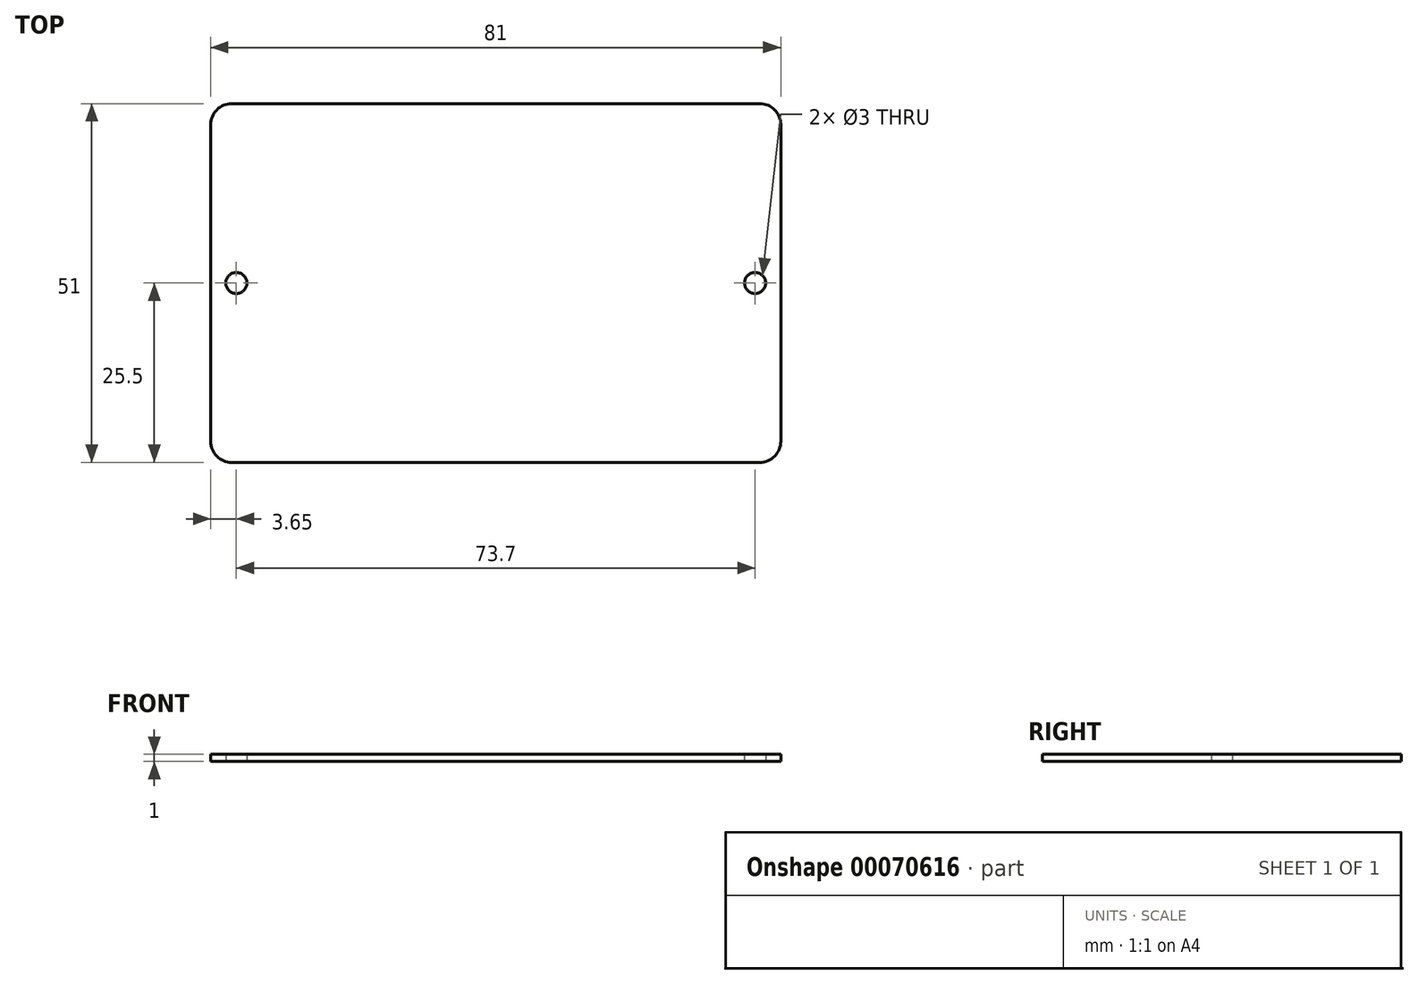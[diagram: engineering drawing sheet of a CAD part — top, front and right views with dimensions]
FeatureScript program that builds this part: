
annotation { "Feature Type Name" : "Feature", "Feature Type Description" : "" }
export const myFeature = defineFeature(function(context is Context, id is Id, definition is map)
    precondition{}
    {
        {
            var Q0;
            Q0=qCreatedBy(makeId("Top.planeOp"),FACE);
            var sketch = newSketch(context, id + "F0", { "sketchPlane" : qUnion([Q0])});
            skLineSegment(sketch, "E0.bottom", {"start": v(-37.5, 25.5) * mm, "end": v(37.5, 25.5) * mm});
            skLineSegment(sketch, "E0.top", {"start": v(-37.5, -25.5) * mm, "end": v(37.5, -25.5) * mm});
            skLineSegment(sketch, "E0.left", {"start": v(-40.5, 22.5) * mm, "end": v(-40.5, -22.5) * mm});
            skLineSegment(sketch, "E0.right", {"start": v(40.5, 22.5) * mm, "end": v(40.5, -22.5) * mm});
            skPoint(sketch, "E1", {"position": v(-36.85, 0) * mm});
            skPoint(sketch, "E2", {"position": v(36.85, 0) * mm});
            skPoint(sketch, "E3.visualSharp", {"position": v(-40.5, 25.5) * mm});
            skArc(sketch, "E3.filletArc", {"start": v(-37.5, 25.5) * mm, "mid": v(-39.62, 24.62) * mm, "end": v(-40.5, 22.5) * mm});
            skPoint(sketch, "E4.visualSharp", {"position": v(40.5, 25.5) * mm});
            skArc(sketch, "E4.filletArc", {"start": v(40.5, 22.5) * mm, "mid": v(39.62, 24.62) * mm, "end": v(37.5, 25.5) * mm});
            skPoint(sketch, "E5.visualSharp", {"position": v(40.5, -25.5) * mm});
            skArc(sketch, "E5.filletArc", {"start": v(37.5, -25.5) * mm, "mid": v(39.62, -24.62) * mm, "end": v(40.5, -22.5) * mm});
            skPoint(sketch, "E6.visualSharp", {"position": v(-40.5, -25.5) * mm});
            skArc(sketch, "E6.filletArc", {"start": v(-40.5, -22.5) * mm, "mid": v(-39.62, -24.62) * mm, "end": v(-37.5, -25.5) * mm});
            skSolve(sketch);
        }
        {
            var Q0;
            Q0=makeQuery(id+"F0.imprint","IMPRINT",FACE,{"disambiguationData":[TD([[makeQuery(id+"F0.imprint","IMPRINT",EDGE,{"derivedFrom":sQuery(id+"F0.wireOp",EDGE,"E0.bottom")}),-1.0]])]});
            extrude(context, id + "F1", {"entities" : qUnion([Q0]), "depth" : 1 * mm});
        }
        {
            var Q0;
            Q0=sQuery(id+"F0.wireOp",VERTEX,"E1");
            var Q1;
            Q1=sQuery(id+"F0.wireOp",VERTEX,"E2");
            var Q2;
            Q2=makeQuery(id+"F1.opExtrude","SWEPT_BODY",BODY,{"disambiguationData":[OSD([sQuery(id+"F0.wireOp",EDGE,"E0.bottom"),sQuery(id+"F0.wireOp",EDGE,"E0.top"),sQuery(id+"F0.wireOp",EDGE,"E0.left"),sQuery(id+"F0.wireOp",EDGE,"E0.right")])]});
            hole(context, id + "F2", {"style" : HoleStyle.SIMPLE, "endStyle" : HoleEndStyle.THROUGH, "oppositeDirection" : true, "holeDiameter" : 3 * mm, "locations" : qUnion([Q0, Q1]), "scope" : qUnion([Q2]), "isTappedThrough" : true});
        }
    });
